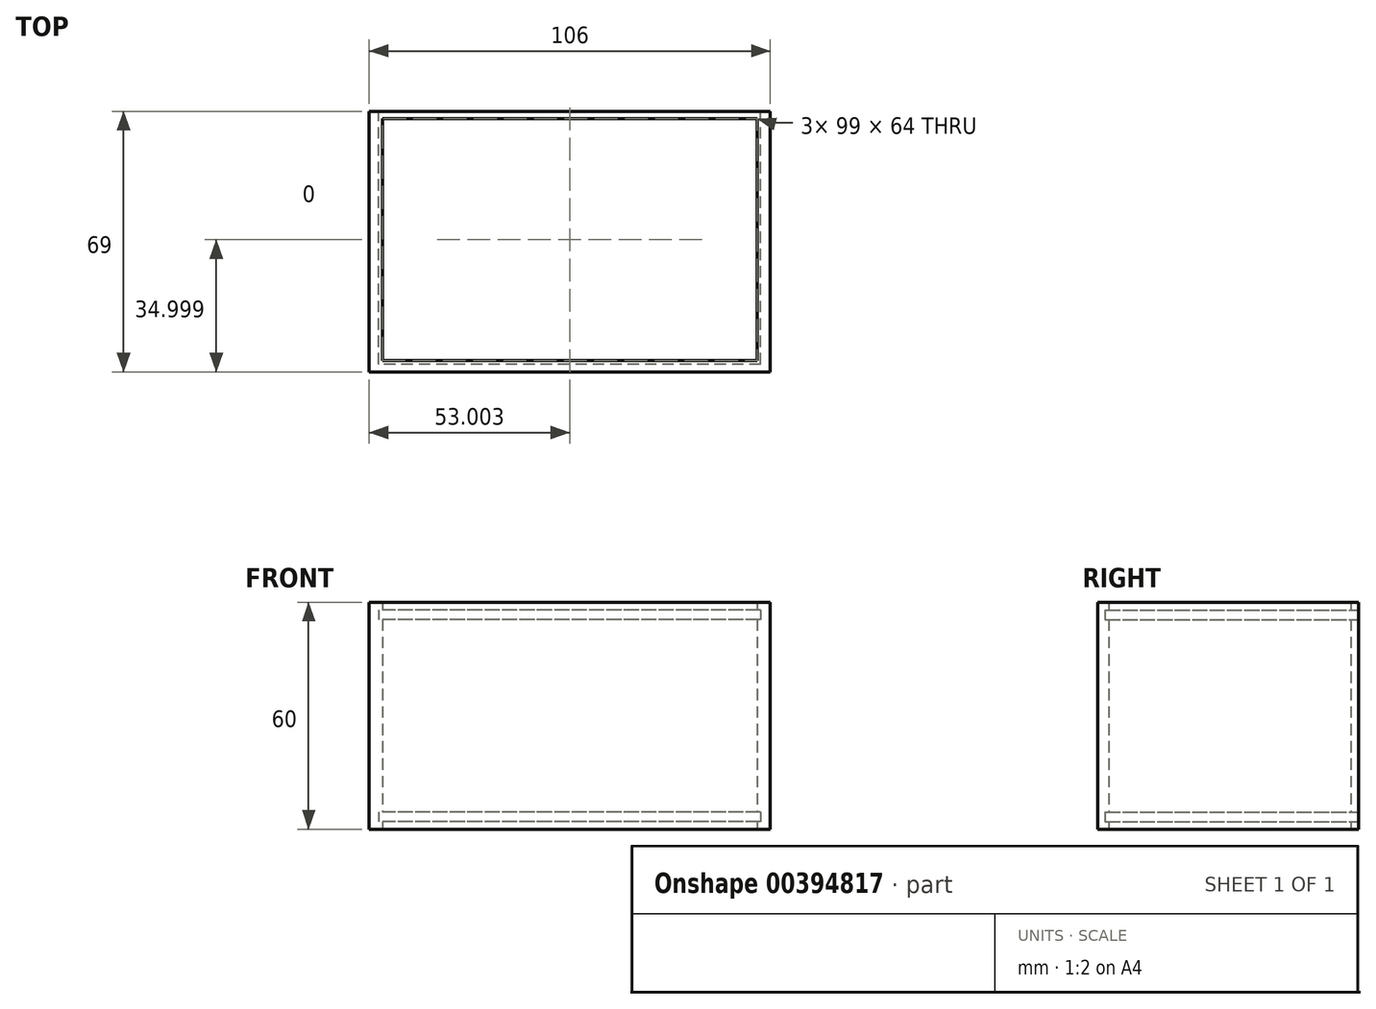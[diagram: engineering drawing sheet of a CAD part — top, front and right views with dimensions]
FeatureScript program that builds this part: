
annotation { "Feature Type Name" : "Feature", "Feature Type Description" : "" }
export const myFeature = defineFeature(function(context is Context, id is Id, definition is map)
    precondition{}
    {
        {
            var Q0;
            Q0=qCreatedBy(makeId("Top.planeOp"),FACE);
            var sketch = newSketch(context, id + "F0", { "sketchPlane" : qUnion([Q0])});
            skLineSegment(sketch, "E0.bottom", {"start": v(-48.76, 31.56) * mm, "end": v(57.24, 31.56) * mm});
            skLineSegment(sketch, "E0.top", {"start": v(-48.76, -37.44) * mm, "end": v(57.24, -37.44) * mm});
            skLineSegment(sketch, "E0.left", {"start": v(-48.76, 31.56) * mm, "end": v(-48.76, -37.44) * mm});
            skLineSegment(sketch, "E0.right", {"start": v(57.24, 31.56) * mm, "end": v(57.24, -37.44) * mm});
            skLineSegment(sketch, "E1.bottom", {"start": v(-45.26, 29.56) * mm, "end": v(53.74, 29.56) * mm});
            skLineSegment(sketch, "E1.top", {"start": v(-45.26, -34.44) * mm, "end": v(53.74, -34.44) * mm});
            skLineSegment(sketch, "E1.left", {"start": v(-45.26, 29.56) * mm, "end": v(-45.26, -34.44) * mm});
            skLineSegment(sketch, "E1.right", {"start": v(53.74, 29.56) * mm, "end": v(53.74, -34.44) * mm});
            skSolve(sketch);
        }
        {
            var Q0;
            Q0=makeQuery(id+"F0.imprint","IMPRINT",FACE,{"disambiguationData":[TD([[makeQuery(id+"F0.imprint","IMPRINT",EDGE,{"derivedFrom":sQuery(id+"F0.wireOp",EDGE,"E0.bottom")}),-1.0]])]});
            extrude(context, id + "F1", {"entities" : qUnion([Q0]), "depth" : 60 * mm});
        }
        {
            var Q0;
            Q0=makeQuery(id+"F1.opExtrude","SWEPT_FACE",FACE,{"disambiguationData":[OSD([sQuery(id+"F0.wireOp",EDGE,"E0.bottom")])]});
            var sketch = newSketch(context, id + "F2", { "sketchPlane" : qUnion([Q0])});
            skLineSegment(sketch, "E2.bottom", {"start": v(-54.74, 58) * mm, "end": v(46.26, 58) * mm});
            skLineSegment(sketch, "E2.top", {"start": v(-54.74, 55.5) * mm, "end": v(46.26, 55.5) * mm});
            skLineSegment(sketch, "E2.left", {"start": v(-54.74, 58) * mm, "end": v(-54.74, 55.5) * mm});
            skLineSegment(sketch, "E2.right", {"start": v(46.26, 58) * mm, "end": v(46.26, 55.5) * mm});
            skLineSegment(sketch, "E3.bottom", {"start": v(-54.74, 4.5) * mm, "end": v(46.26, 4.5) * mm});
            skLineSegment(sketch, "E3.top", {"start": v(-54.74, 2) * mm, "end": v(46.26, 2) * mm});
            skLineSegment(sketch, "E3.left", {"start": v(-54.74, 4.5) * mm, "end": v(-54.74, 2) * mm});
            skLineSegment(sketch, "E3.right", {"start": v(46.26, 4.5) * mm, "end": v(46.26, 2) * mm});
            skSolve(sketch);
        }
        {
            var Q0;
            Q0 = qSketchRegion(id + "F2", true);
            extrude(context, id + "F3", {"entities" : qUnion([Q0]), "operationType" : NewBodyOperationType.REMOVE, "oppositeDirection" : true, "depth" : 67 * mm});
        }
    });
